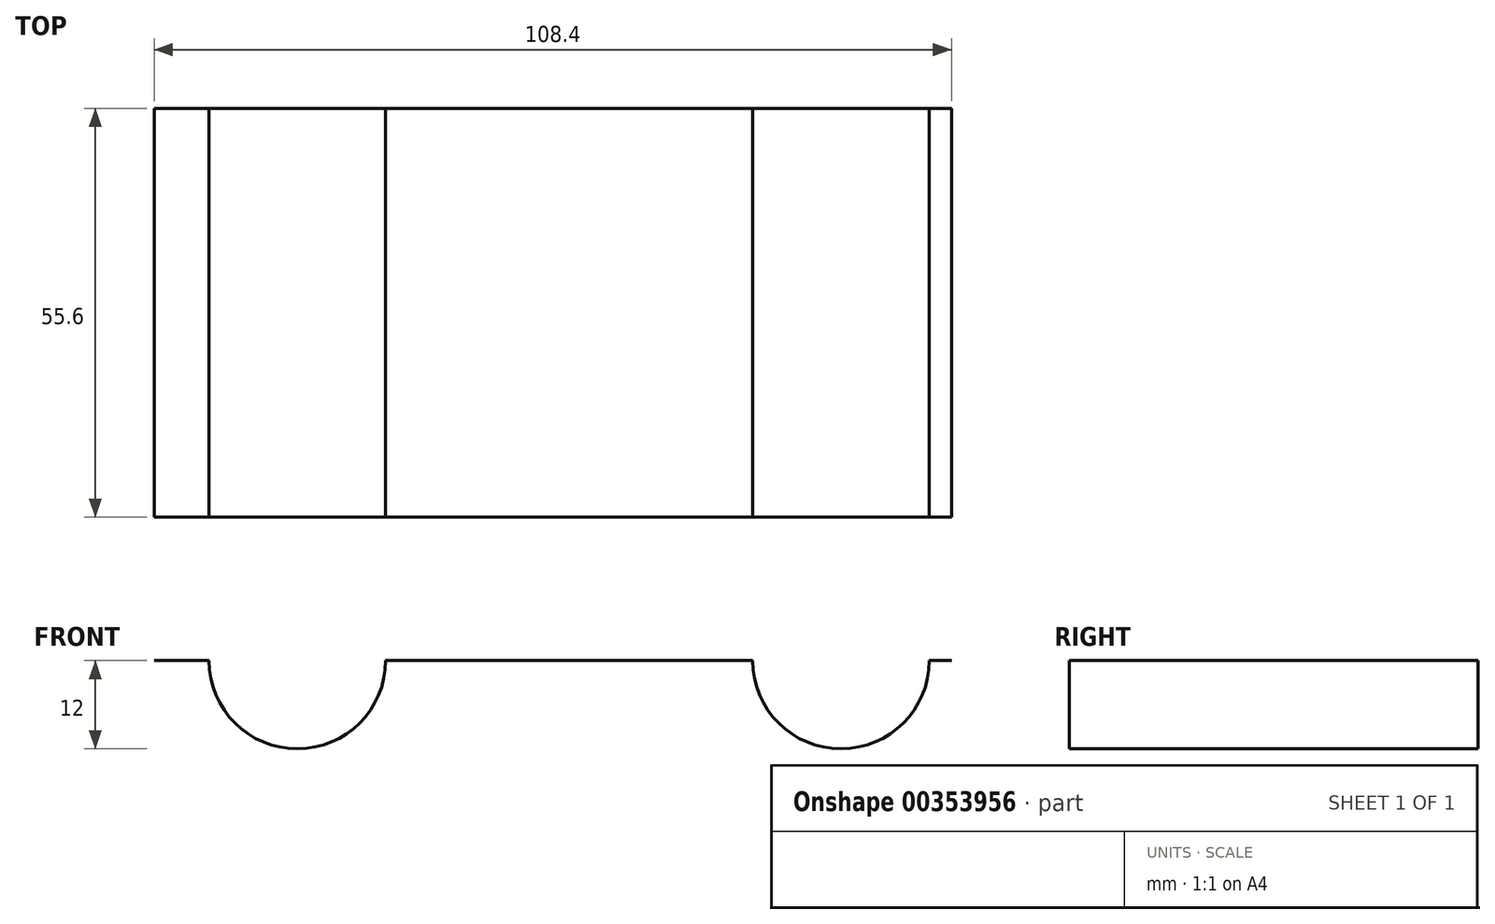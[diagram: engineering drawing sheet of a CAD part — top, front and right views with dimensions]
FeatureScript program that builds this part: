
annotation { "Feature Type Name" : "Feature", "Feature Type Description" : "" }
export const myFeature = defineFeature(function(context is Context, id is Id, definition is map)
    precondition{}
    {
        {
            var Q0;
            Q0=qCreatedBy(makeId("Front.planeOp"),FACE);
            var sketch = newSketch(context, id + "F0", { "sketchPlane" : qUnion([Q0])});
            skLineSegment(sketch, "E0", {"start": v(52.73, 0) * mm, "end": v(49.7, 0) * mm});
            skArc(sketch, "E1", {"start": v(25.7, 0) * mm, "mid": v(37.7, -12) * mm, "end": v(49.7, 0) * mm});
            skArc(sketch, "E2", {"start": v(-48.2, 0) * mm, "mid": v(-36.2, -12) * mm, "end": v(-24.2, 0) * mm});
            skLineSegment(sketch, "E3.trimOffspring", {"start": v(25.7, 0) * mm, "end": v(-24.2, 0) * mm});
            skLineSegment(sketch, "E4.trimOffspring", {"start": v(-48.2, 0) * mm, "end": v(-55.67, 0) * mm});
            skSolve(sketch);
        }
        {
            var Q0;
            Q0=sQuery(id+"F0.wireOp",EDGE,"E4.trimOffspring");
            var Q1;
            Q1=sQuery(id+"F0.wireOp",EDGE,"E2");
            var Q2;
            Q2=sQuery(id+"F0.wireOp",EDGE,"E3.trimOffspring");
            var Q3;
            Q3=sQuery(id+"F0.wireOp",EDGE,"E1");
            var Q4;
            Q4=sQuery(id+"F0.wireOp",EDGE,"E0");
            extrude(context, id + "F1", {"bodyType" : ToolBodyType.SURFACE, "surfaceEntities" : qUnion([Q0, Q1, Q2, Q3, Q4]), "endBound" : BoundingType.SYMMETRIC, "depth" : 55.6 * mm});
        }
    });
